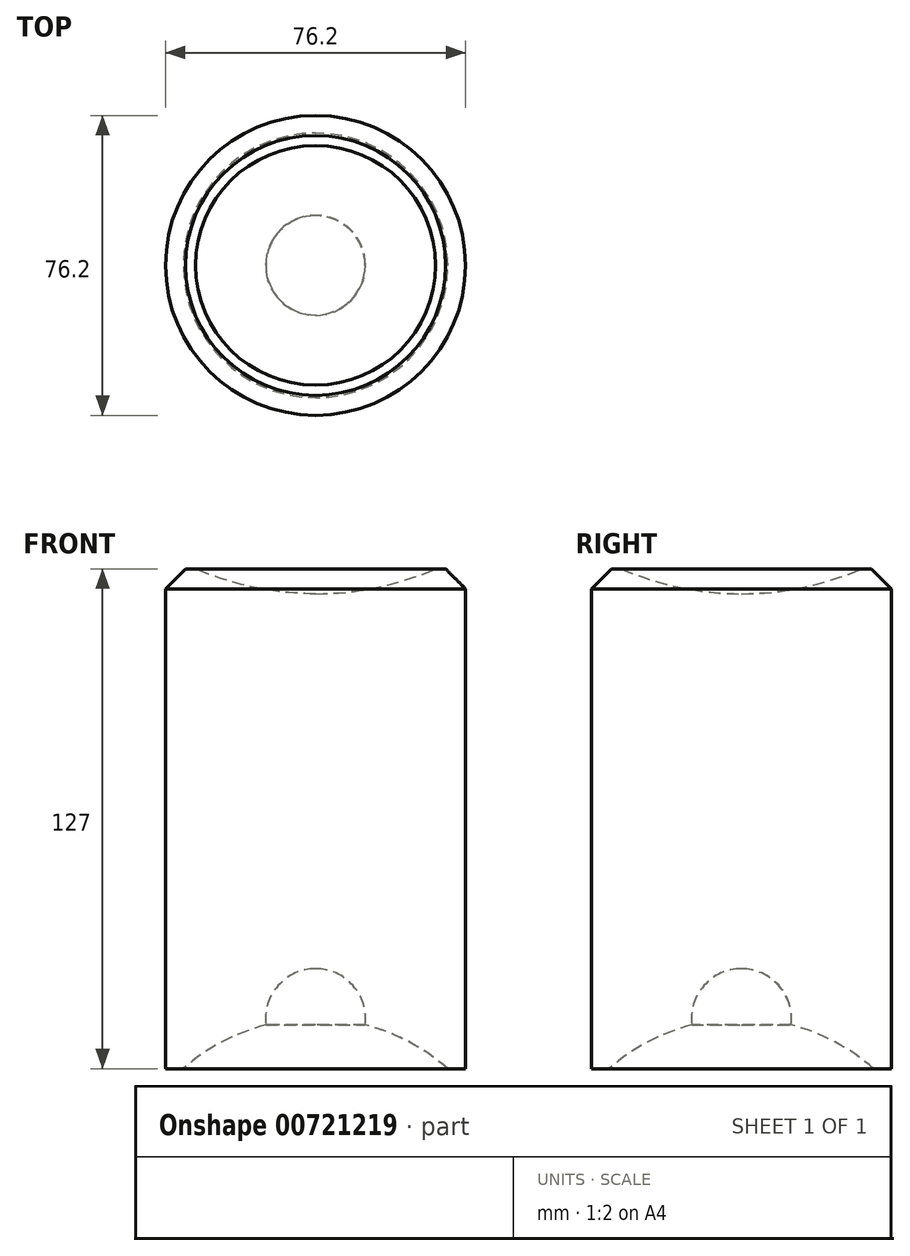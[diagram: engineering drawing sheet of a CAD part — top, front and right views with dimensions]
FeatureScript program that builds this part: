
annotation { "Feature Type Name" : "Feature", "Feature Type Description" : "" }
export const myFeature = defineFeature(function(context is Context, id is Id, definition is map)
    precondition{}
    {
        {
            var Q0;
            Q0=qCreatedBy(makeId("Front.planeOp"),FACE);
            var sketch = newSketch(context, id + "F0", { "sketchPlane" : qUnion([Q0])});
            skLineSegment(sketch, "E0.bottom", {"start": v(0, 63.5) * mm, "end": v(-38.1, 63.5) * mm});
            skLineSegment(sketch, "E0.top", {"start": v(0, -63.5) * mm, "end": v(-38.1, -63.5) * mm});
            skLineSegment(sketch, "E0.left", {"start": v(0, 63.5) * mm, "end": v(0, -63.5) * mm});
            skLineSegment(sketch, "E0.right", {"start": v(-38.1, 63.5) * mm, "end": v(-38.1, -63.5) * mm});
            skArc(sketch, "E1", {"start": v(-30.45, 63.5) * mm, "mid": v(-15.55, 58.75) * mm, "end": v(0, 57.15) * mm});
            skSolve(sketch);
        }
        {
            var Q0;
            {var subQ2=sQuery(id+"F0.wireOp",EDGE,"E0.top");Q0=makeQuery(id+"F0.imprint","IMPRINT",FACE,{"disambiguationData":[TD([[makeQuery(id+"F0.imprint","IMPRINT",EDGE,{"derivedFrom":subQ2}),-1.0]])]});}
            var Q1;
            Q1=sQuery(id+"F0.wireOp",EDGE,"E0.left");
            revolve(context, id + "F1", {"surfaceOperationType" : NewSurfaceOperationType.NEW, "entities" : qUnion([Q0]), "axis" : qUnion([Q1]), "revolveType" : RevolveType.FULL});
        }
        {
            var Q0;
            Q0=makeQuery(id+"F1.opRevolve","SWEPT_EDGE",EDGE,{"disambiguationData":[OSD([sQuery(id+"F0.wireOp",EDGE,"E0.bottom"),sQuery(id+"F0.wireOp",EDGE,"E0.right")])]});
            chamfer(context, id + "F2", {"entities" : qUnion([Q0]), "width" : 5.08 * mm, "tangentPropagation" : true});
        }
        {
            var Q0;
            Q0=qCreatedBy(makeId("Right.planeOp"),FACE);
            var sketch = newSketch(context, id + "F3", { "sketchPlane" : qUnion([Q0])});
            skArc(sketch, "E2", {"start": v(-12.6, -52.39) * mm, "mid": v(-50.4, -107.95) * mm, "end": v(0, -152.4) * mm});
            skArc(sketch, "E3", {"start": v(0, -38.1) * mm, "mid": v(-9.53, -42.4) * mm, "end": v(-12.6, -52.39) * mm});
            skLineSegment(sketch, "E4", {"start": v(0, -38.1) * mm, "end": v(0, -152.4) * mm});
            skSolve(sketch);
        }
        {
            var Q0;
            Q0 = qSketchRegion(id + "F3", true);
            var Q1;
            Q1=sQuery(id+"F3.wireOp",EDGE,"E4");
            revolve(context, id + "F4", {"operationType" : NewBodyOperationType.REMOVE, "surfaceOperationType" : NewSurfaceOperationType.NEW, "entities" : qUnion([Q0]), "axis" : qUnion([Q1]), "revolveType" : RevolveType.FULL});
        }
    });
